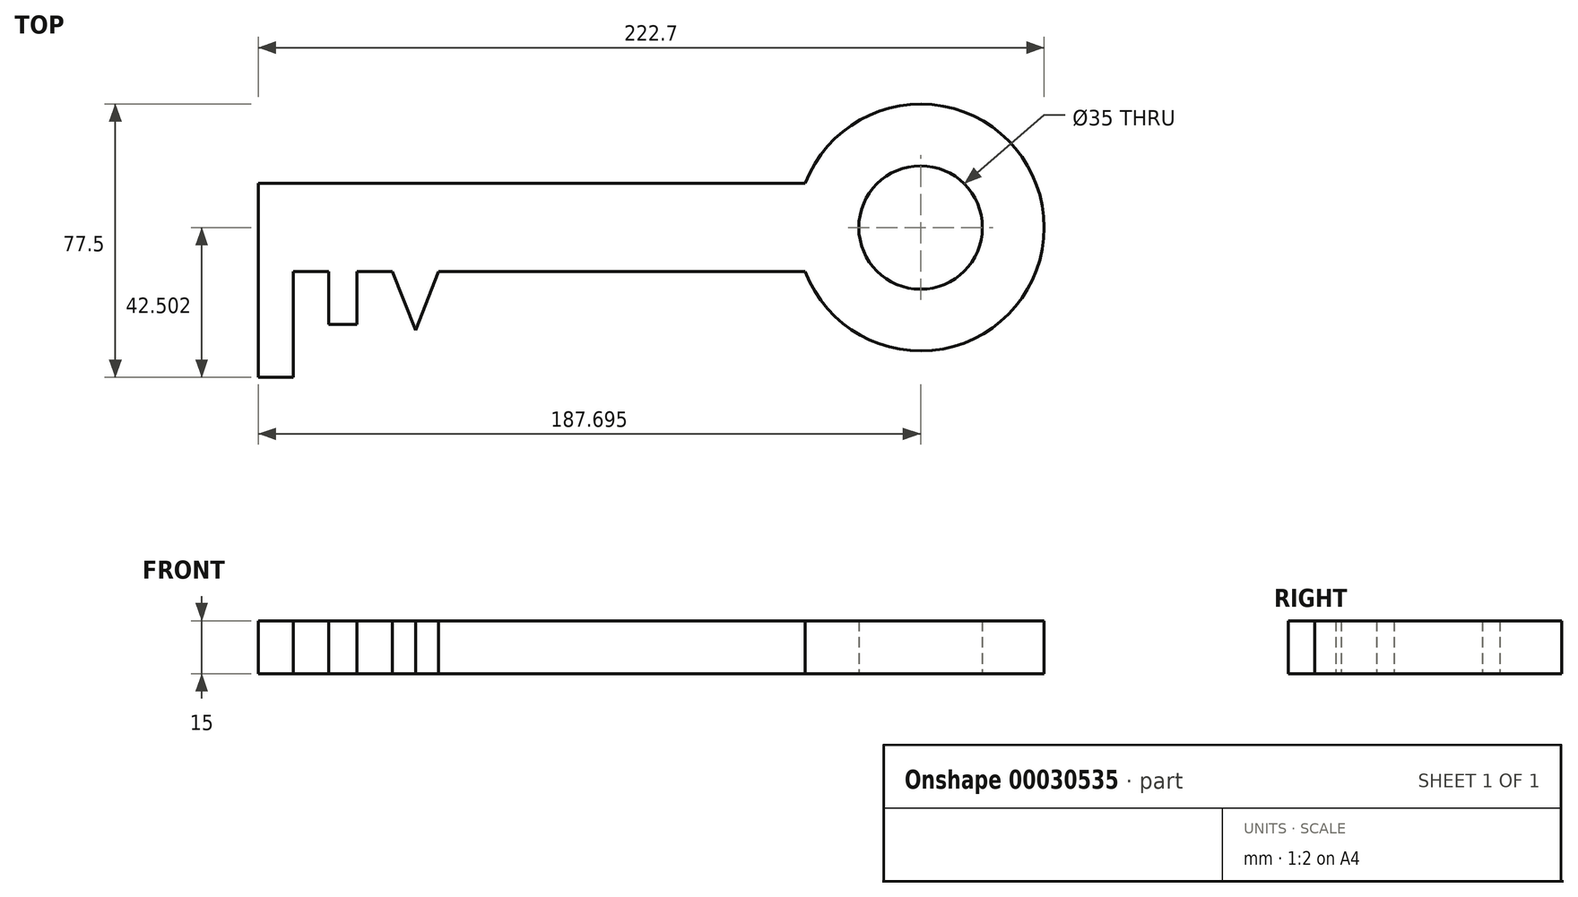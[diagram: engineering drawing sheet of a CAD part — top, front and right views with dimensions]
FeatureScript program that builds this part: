
annotation { "Feature Type Name" : "Feature", "Feature Type Description" : "" }
export const myFeature = defineFeature(function(context is Context, id is Id, definition is map)
    precondition{}
    {
        {
            var Q0;
            Q0=qCreatedBy(makeId("Top.planeOp"),FACE);
            var sketch = newSketch(context, id + "F0", { "sketchPlane" : qUnion([Q0])});
            skLineSegment(sketch, "E0.bottom", {"start": v(-99.46, 19.41) * mm, "end": v(55.54, 19.41) * mm});
            skLineSegment(sketch, "E0.top", {"start": v(-89.46, -5.59) * mm, "end": v(-79.46, -5.59) * mm});
            skLineSegment(sketch, "E0.left", {"start": v(-99.46, 19.41) * mm, "end": v(-99.46, -5.59) * mm});
            skLineSegment(sketch, "E1.top", {"start": v(-99.46, -35.59) * mm, "end": v(-89.46, -35.59) * mm});
            skLineSegment(sketch, "E1.left", {"start": v(-99.46, -5.59) * mm, "end": v(-99.46, -35.59) * mm});
            skLineSegment(sketch, "E1.right", {"start": v(-89.46, -5.59) * mm, "end": v(-89.46, -35.59) * mm});
            skLineSegment(sketch, "E2.top", {"start": v(-79.46, -20.59) * mm, "end": v(-71.46, -20.59) * mm});
            skLineSegment(sketch, "E2.left", {"start": v(-79.46, -5.59) * mm, "end": v(-79.46, -20.59) * mm});
            skLineSegment(sketch, "E2.right", {"start": v(-71.46, -5.59) * mm, "end": v(-71.46, -20.59) * mm});
            skLineSegment(sketch, "E3", {"start": v(-61.46, -5.59) * mm, "end": v(-54.88, -22.15) * mm});
            skLineSegment(sketch, "E4", {"start": v(-54.88, -22.15) * mm, "end": v(-48.3, -5.59) * mm});
            skArc(sketch, "E5", {"start": v(55.54, -5.59) * mm, "mid": v(123.24, 6.91) * mm, "end": v(55.54, 19.41) * mm});
            skCircle(sketch, "E6", {"center": v(88.24, 6.91) * mm, "radius": 17.5 * mm});
            skLineSegment(sketch, "E7", {"start": v(-99.46, 6.91) * mm, "end": v(88.24, 6.91) * mm, "construction": true});
            skLineSegment(sketch, "E8.trimOffspring", {"start": v(-71.46, -5.59) * mm, "end": v(-61.46, -5.59) * mm});
            skLineSegment(sketch, "E9.trimOffspring", {"start": v(-48.3, -5.59) * mm, "end": v(55.54, -5.59) * mm});
            skSolve(sketch);
        }
        {
            var Q0;
            Q0=makeQuery(id+"F0.imprint","IMPRINT",FACE,{"disambiguationData":[TD([[makeQuery(id+"F0.imprint","IMPRINT",EDGE,{"derivedFrom":sQuery(id+"F0.wireOp",EDGE,"E0.bottom")}),-1.0]])]});
            extrude(context, id + "F1", {"entities" : qUnion([Q0]), "depth" : 15 * mm});
        }
    });
